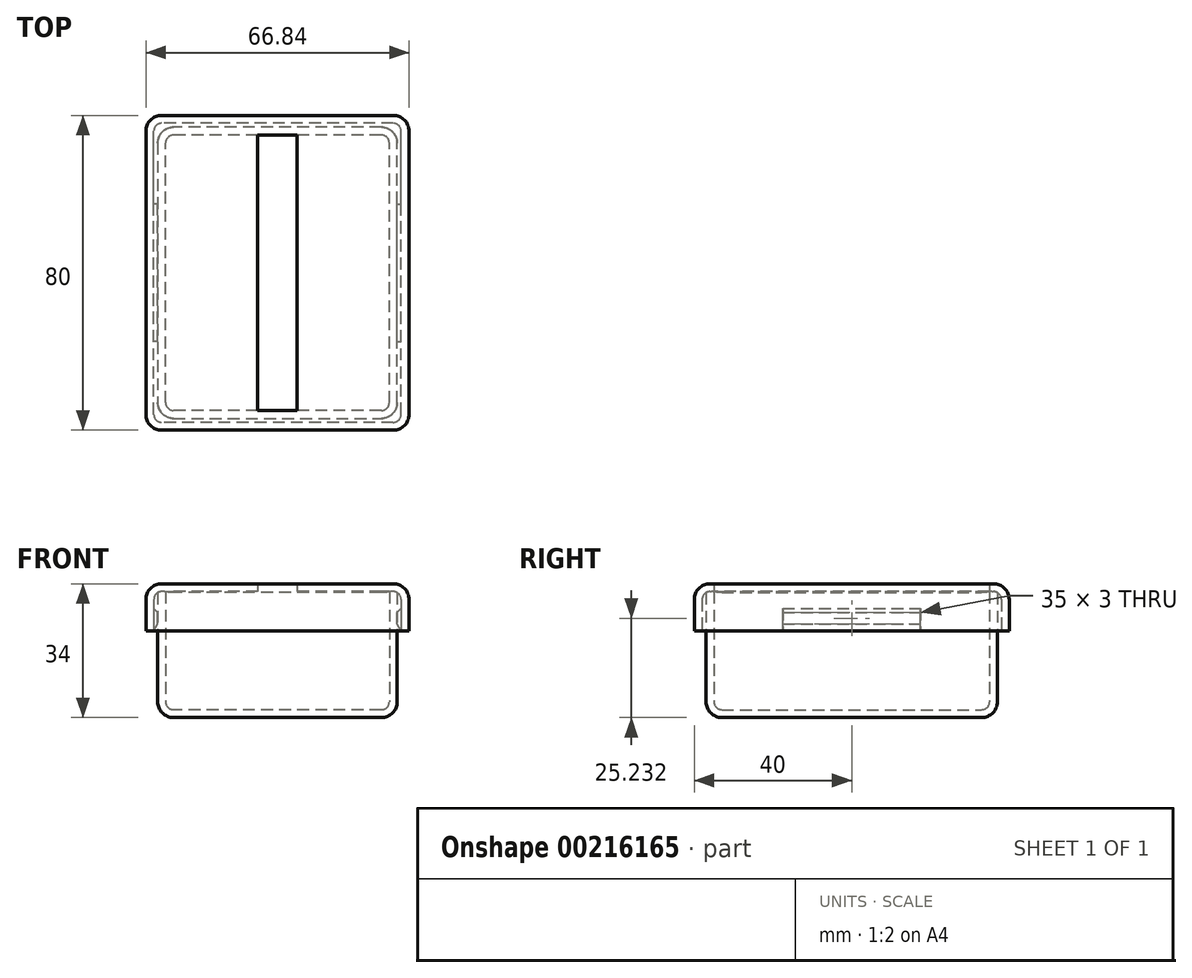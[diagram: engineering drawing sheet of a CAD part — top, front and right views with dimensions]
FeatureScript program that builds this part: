
annotation { "Feature Type Name" : "Feature", "Feature Type Description" : "" }
export const myFeature = defineFeature(function(context is Context, id is Id, definition is map)
    precondition{}
    {
        {
            assignVariable(context, id + "F0", {"name" : "BILL_WIDTH", "anyValue" : 70});
        }
        {
            assignVariable(context, id + "F1", {"name" : "THICKNESS", "anyValue" : 2});
        }
        {
            var Q0;
            Q0=qCreatedBy(makeId("Top.planeOp"),FACE);
            cPlane(context, id + "F2", {"entities" : qUnion([Q0]), "cplaneType" : CPlaneType.OFFSET, "offset" : (30 + getVariable(context, 'THICKNESS')) * mm, "width" : 150 * mm, "height" : 150 * mm});
        }
        {
            var Q0;
            Q0=qCreatedBy(makeId("Top.planeOp"),FACE);
            var sketch = newSketch(context, id + "F3", { "sketchPlane" : qUnion([Q0])});
            skLineSegment(sketch, "E0.bottom", {"start": v(30.42, -37) * mm, "end": v(-30.42, -37) * mm});
            skLineSegment(sketch, "E0.top", {"start": v(30.42, 37) * mm, "end": v(-30.42, 37) * mm});
            skLineSegment(sketch, "E0.left", {"start": v(30.42, -37) * mm, "end": v(30.42, 37) * mm});
            skLineSegment(sketch, "E0.right", {"start": v(-30.42, -37) * mm, "end": v(-30.42, 37) * mm});
            skPoint(sketch, "E0.middle", {"position": v(0, 0) * mm});
            skSolve(sketch);
        }
        {
            var Q0;
            Q0 = qSketchRegion(id + "F3", true);
            var Q1;
            Q1=qCreatedBy(id+"F2.planeOp",FACE);
            extrude(context, id + "F4", {"entities" : qUnion([Q0]), "endBound" : BoundingType.UP_TO_SURFACE, "endBoundEntityFace" : qUnion([Q1]), "depth" : 25 * mm});
        }
        {
            var Q0;
            Q0=makeQuery(id+"F4.opExtrude","CAP_FACE",FACE,{"disambiguationData":[OSD([sQuery(id+"F3.wireOp",EDGE,"E0.bottom"),sQuery(id+"F3.wireOp",EDGE,"E0.top"),sQuery(id+"F3.wireOp",EDGE,"E0.left"),sQuery(id+"F3.wireOp",EDGE,"E0.right")])],"isStart":false});
            shell(context, id + "F5", {"entities" : qUnion([Q0]), "thickness" : (getVariable(context, 'THICKNESS')) * mm});
        }
        {
            var Q0;
            Q0=makeQuery(id+"F5.opShell","OFFSET_FACE",FACE,{"disambiguationData":[OSD([sQuery(id+"F3.wireOp",EDGE,"E0.bottom"),sQuery(id+"F3.wireOp",EDGE,"E0.top"),sQuery(id+"F3.wireOp",EDGE,"E0.left"),sQuery(id+"F3.wireOp",EDGE,"E0.right")])]});
            var Q1;
            Q1=makeQuery(id+"F5.opShell","OFFSET_EDGE",EDGE,{"disambiguationData":[OSD([sQuery(id+"F3.wireOp",EDGE,"E0.bottom"),sQuery(id+"F3.wireOp",EDGE,"E0.left")])]});
            var Q2;
            Q2=makeQuery(id+"F5.opShell","OFFSET_EDGE",EDGE,{"disambiguationData":[OSD([sQuery(id+"F3.wireOp",EDGE,"E0.top"),sQuery(id+"F3.wireOp",EDGE,"E0.left")])]});
            var Q3;
            Q3=makeQuery(id+"F5.opShell","OFFSET_EDGE",EDGE,{"disambiguationData":[OSD([sQuery(id+"F3.wireOp",EDGE,"E0.top"),sQuery(id+"F3.wireOp",EDGE,"E0.right")])]});
            var Q4;
            Q4=makeQuery(id+"F5.opShell","OFFSET_EDGE",EDGE,{"disambiguationData":[OSD([sQuery(id+"F3.wireOp",EDGE,"E0.bottom"),sQuery(id+"F3.wireOp",EDGE,"E0.right")])]});
            fillet(context, id + "F6", {"entities" : qUnion([Q0, Q1, Q2, Q3, Q4]), "radius" : (getVariable(context, 'THICKNESS')) * mm, "tangentPropagation" : true, "allowEdgeOverflow" : false});
        }
        {
            var Q0;
            Q0=makeQuery(id+"F4.opExtrude","CAP_FACE",FACE,{"disambiguationData":[OSD([sQuery(id+"F3.wireOp",EDGE,"E0.bottom"),sQuery(id+"F3.wireOp",EDGE,"E0.top"),sQuery(id+"F3.wireOp",EDGE,"E0.left"),sQuery(id+"F3.wireOp",EDGE,"E0.right")])],"isStart":true});
            var Q1;
            Q1=makeQuery(id+"F4.opExtrude","SWEPT_EDGE",EDGE,{"disambiguationData":[OSD([sQuery(id+"F3.wireOp",EDGE,"E0.bottom"),sQuery(id+"F3.wireOp",EDGE,"E0.left")])]});
            var Q2;
            Q2=makeQuery(id+"F4.opExtrude","SWEPT_EDGE",EDGE,{"disambiguationData":[OSD([sQuery(id+"F3.wireOp",EDGE,"E0.top"),sQuery(id+"F3.wireOp",EDGE,"E0.left")])]});
            var Q3;
            Q3=makeQuery(id+"F4.opExtrude","SWEPT_EDGE",EDGE,{"disambiguationData":[OSD([sQuery(id+"F3.wireOp",EDGE,"E0.bottom"),sQuery(id+"F3.wireOp",EDGE,"E0.right")])]});
            var Q4;
            Q4=makeQuery(id+"F4.opExtrude","SWEPT_EDGE",EDGE,{"disambiguationData":[OSD([sQuery(id+"F3.wireOp",EDGE,"E0.top"),sQuery(id+"F3.wireOp",EDGE,"E0.right")])]});
            fillet(context, id + "F7", {"entities" : qUnion([Q0, Q1, Q2, Q3, Q4]), "radius" : (getVariable(context, 'THICKNESS') * 2) * mm, "tangentPropagation" : true, "allowEdgeOverflow" : false});
        }
        {
            var Q0;
            Q0=qCreatedBy(id+"F2.planeOp",FACE);
            var sketch = newSketch(context, id + "F8", { "sketchPlane" : qUnion([Q0])});
            skLineSegment(sketch, "E1.bottom", {"start": v(33.42, -40) * mm, "end": v(-33.42, -40) * mm});
            skLineSegment(sketch, "E1.top", {"start": v(33.42, 40) * mm, "end": v(-33.42, 40) * mm});
            skLineSegment(sketch, "E1.left", {"start": v(33.42, -40) * mm, "end": v(33.42, 40) * mm});
            skLineSegment(sketch, "E1.right", {"start": v(-33.42, -40) * mm, "end": v(-33.42, 40) * mm});
            skPoint(sketch, "E1.middle", {"position": v(0, 0) * mm});
            skSolve(sketch);
        }
        {
            var Q0;
            Q0 = qSketchRegion(id + "F8", true);
            extrude(context, id + "F9", {"entities" : qUnion([Q0]), "depth" : (getVariable(context, 'THICKNESS')) * mm, "hasSecondDirection" : true, "secondDirectionOppositeDirection" : true, "secondDirectionDepth" : 10 * mm});
        }
        {
            var Q0;
            Q0=makeQuery(id+"F9.opExtrude","CAP_FACE",FACE,{"disambiguationData":[OSD([sQuery(id+"F8.wireOp",EDGE,"E1.bottom"),sQuery(id+"F8.wireOp",EDGE,"E1.top"),sQuery(id+"F8.wireOp",EDGE,"E1.left"),sQuery(id+"F8.wireOp",EDGE,"E1.right")])],"isStart":true});
            shell(context, id + "F10", {"entities" : qUnion([Q0]), "thickness" : (getVariable(context, 'THICKNESS')) * mm});
        }
        {
            var Q0;
            Q0=qCreatedBy(id+"F2.planeOp",FACE);
            var sketch = newSketch(context, id + "F11", { "sketchPlane" : qUnion([Q0])});
            skLineSegment(sketch, "E2.bottom", {"start": v(5, 35) * mm, "end": v(-5, 35) * mm});
            skLineSegment(sketch, "E2.top", {"start": v(5, -35) * mm, "end": v(-5, -35) * mm});
            skLineSegment(sketch, "E2.left", {"start": v(5, 35) * mm, "end": v(5, -35) * mm});
            skLineSegment(sketch, "E2.right", {"start": v(-5, 35) * mm, "end": v(-5, -35) * mm});
            skPoint(sketch, "E2.middle", {"position": v(0, 0) * mm});
            skSolve(sketch);
        }
        {
            var Q0;
            Q0 = qSketchRegion(id + "F11", true);
            extrude(context, id + "F12", {"entities" : qUnion([Q0]), "operationType" : NewBodyOperationType.REMOVE, "endBound" : BoundingType.THROUGH_ALL, "depth" : 25 * mm});
        }
        {
            var Q0;
            Q0=qCreatedBy(makeId("Front.planeOp"),FACE);
            var sketch = newSketch(context, id + "F13", { "sketchPlane" : qUnion([Q0])});
            skLineSegment(sketch, "E3.0", {"start": v(-31.42, 27.73) * mm, "end": v(-31.42, 22) * mm});
            skLineSegment(sketch, "E4.0", {"start": v(31.42, 27.73) * mm, "end": v(31.42, 22) * mm});
            skLineSegment(sketch, "E5", {"start": v(-31.42, 22) * mm, "end": v(-30.42, 23.73) * mm});
            skLineSegment(sketch, "E6", {"start": v(-30.42, 23.73) * mm, "end": v(-30.42, 26.73) * mm});
            skLineSegment(sketch, "E7", {"start": v(31.42, 22) * mm, "end": v(30.42, 23.73) * mm});
            skLineSegment(sketch, "E8", {"start": v(30.42, 23.73) * mm, "end": v(30.42, 26.73) * mm});
            skLineSegment(sketch, "E9", {"start": v(30.42, 26.73) * mm, "end": v(31.42, 27.73) * mm});
            skLineSegment(sketch, "E10", {"start": v(-30.42, 26.73) * mm, "end": v(-31.42, 27.73) * mm});
            skSolve(sketch);
        }
        {
            var Q0;
            Q0 = qSketchRegion(id + "F13", true);
            extrude(context, id + "F14", {"entities" : qUnion([Q0]), "operationType" : NewBodyOperationType.ADD, "endBound" : BoundingType.SYMMETRIC, "depth" : (getVariable(context, 'BILL_WIDTH') / 2) * mm});
        }
        {
            var Q0;
            {var subQ0=sQuery(id+"F8.wireOp",EDGE,"E1.bottom");Q0=makeQuery(id+"F10.opShell","OFFSET_EDGE",EDGE,{"disambiguationData":[OSD([subQ0]),TDD([makeQuery(id+"F9.opExtrude","CAP_EDGE",EDGE,{"disambiguationData":[OSD([subQ0])],"isStart":false})])]});}
            var Q1;
            {var subQ0=sQuery(id+"F8.wireOp",EDGE,"E1.right");Q1=makeQuery(id+"F10.opShell","OFFSET_EDGE",EDGE,{"disambiguationData":[OSD([subQ0]),TDD([makeQuery(id+"F9.opExtrude","CAP_EDGE",EDGE,{"disambiguationData":[OSD([subQ0])],"isStart":false})])]});}
            var Q2;
            {var subQ0=sQuery(id+"F8.wireOp",EDGE,"E1.top");Q2=makeQuery(id+"F10.opShell","OFFSET_EDGE",EDGE,{"disambiguationData":[OSD([subQ0]),TDD([makeQuery(id+"F9.opExtrude","CAP_EDGE",EDGE,{"disambiguationData":[OSD([subQ0])],"isStart":false})])]});}
            var Q3;
            {var subQ0=sQuery(id+"F8.wireOp",EDGE,"E1.left");Q3=makeQuery(id+"F10.opShell","OFFSET_EDGE",EDGE,{"disambiguationData":[OSD([subQ0]),TDD([makeQuery(id+"F9.opExtrude","CAP_EDGE",EDGE,{"disambiguationData":[OSD([subQ0])],"isStart":false})])]});}
            var Q4;
            Q4=makeQuery(id+"F12.boolean.opBoolean","COPY",EDGE,{"derivedFrom":makeQuery(id+"F12.opExtrude","CAP_EDGE",EDGE,{"disambiguationData":[OSD([sQuery(id+"F11.wireOp",EDGE,"E2.left")])],"isStart":true})});
            var Q5;
            Q5=makeQuery(id+"F12.boolean.opBoolean","COPY",EDGE,{"derivedFrom":makeQuery(id+"F12.opExtrude","CAP_EDGE",EDGE,{"disambiguationData":[OSD([sQuery(id+"F11.wireOp",EDGE,"E2.right")])],"isStart":true})});
            var Q6;
            Q6=makeQuery(id+"F10.opShell","OFFSET_EDGE",EDGE,{"disambiguationData":[OSD([sQuery(id+"F8.wireOp",EDGE,"E1.bottom"),sQuery(id+"F8.wireOp",EDGE,"E1.right")])]});
            var Q7;
            Q7=makeQuery(id+"F10.opShell","OFFSET_EDGE",EDGE,{"disambiguationData":[OSD([sQuery(id+"F8.wireOp",EDGE,"E1.bottom"),sQuery(id+"F8.wireOp",EDGE,"E1.left")])]});
            var Q8;
            Q8=makeQuery(id+"F10.opShell","OFFSET_EDGE",EDGE,{"disambiguationData":[OSD([sQuery(id+"F8.wireOp",EDGE,"E1.top"),sQuery(id+"F8.wireOp",EDGE,"E1.left")])]});
            var Q9;
            Q9=makeQuery(id+"F10.opShell","OFFSET_EDGE",EDGE,{"disambiguationData":[OSD([sQuery(id+"F8.wireOp",EDGE,"E1.top"),sQuery(id+"F8.wireOp",EDGE,"E1.right")])]});
            fillet(context, id + "F15", {"entities" : qUnion([Q0, Q1, Q2, Q3, Q4, Q5, Q6, Q7, Q8, Q9]), "radius" : (getVariable(context, 'THICKNESS')) * mm, "tangentPropagation" : true, "allowEdgeOverflow" : false});
        }
        {
            var Q0;
            Q0=makeQuery(id+"F9.opExtrude","CAP_EDGE",EDGE,{"disambiguationData":[OSD([sQuery(id+"F8.wireOp",EDGE,"E1.left")])],"isStart":false});
            var Q1;
            Q1=makeQuery(id+"F9.opExtrude","CAP_EDGE",EDGE,{"disambiguationData":[OSD([sQuery(id+"F8.wireOp",EDGE,"E1.right")])],"isStart":false});
            var Q2;
            Q2=makeQuery(id+"F9.opExtrude","CAP_EDGE",EDGE,{"disambiguationData":[OSD([sQuery(id+"F8.wireOp",EDGE,"E1.top")])],"isStart":false});
            var Q3;
            Q3=makeQuery(id+"F9.opExtrude","CAP_EDGE",EDGE,{"disambiguationData":[OSD([sQuery(id+"F8.wireOp",EDGE,"E1.bottom")])],"isStart":false});
            var Q4;
            Q4=makeQuery(id+"F9.opExtrude","SWEPT_EDGE",EDGE,{"disambiguationData":[OSD([sQuery(id+"F8.wireOp",EDGE,"E1.bottom"),sQuery(id+"F8.wireOp",EDGE,"E1.left")])]});
            var Q5;
            Q5=makeQuery(id+"F9.opExtrude","SWEPT_EDGE",EDGE,{"disambiguationData":[OSD([sQuery(id+"F8.wireOp",EDGE,"E1.top"),sQuery(id+"F8.wireOp",EDGE,"E1.left")])]});
            var Q6;
            Q6=makeQuery(id+"F9.opExtrude","SWEPT_EDGE",EDGE,{"disambiguationData":[OSD([sQuery(id+"F8.wireOp",EDGE,"E1.top"),sQuery(id+"F8.wireOp",EDGE,"E1.right")])]});
            var Q7;
            Q7=makeQuery(id+"F9.opExtrude","SWEPT_EDGE",EDGE,{"disambiguationData":[OSD([sQuery(id+"F8.wireOp",EDGE,"E1.bottom"),sQuery(id+"F8.wireOp",EDGE,"E1.right")])]});
            fillet(context, id + "F16", {"entities" : qUnion([Q0, Q1, Q2, Q3, Q4, Q5, Q6, Q7]), "radius" : (getVariable(context, 'THICKNESS') * 2) * mm, "tangentPropagation" : true, "allowEdgeOverflow" : false});
        }
    });
